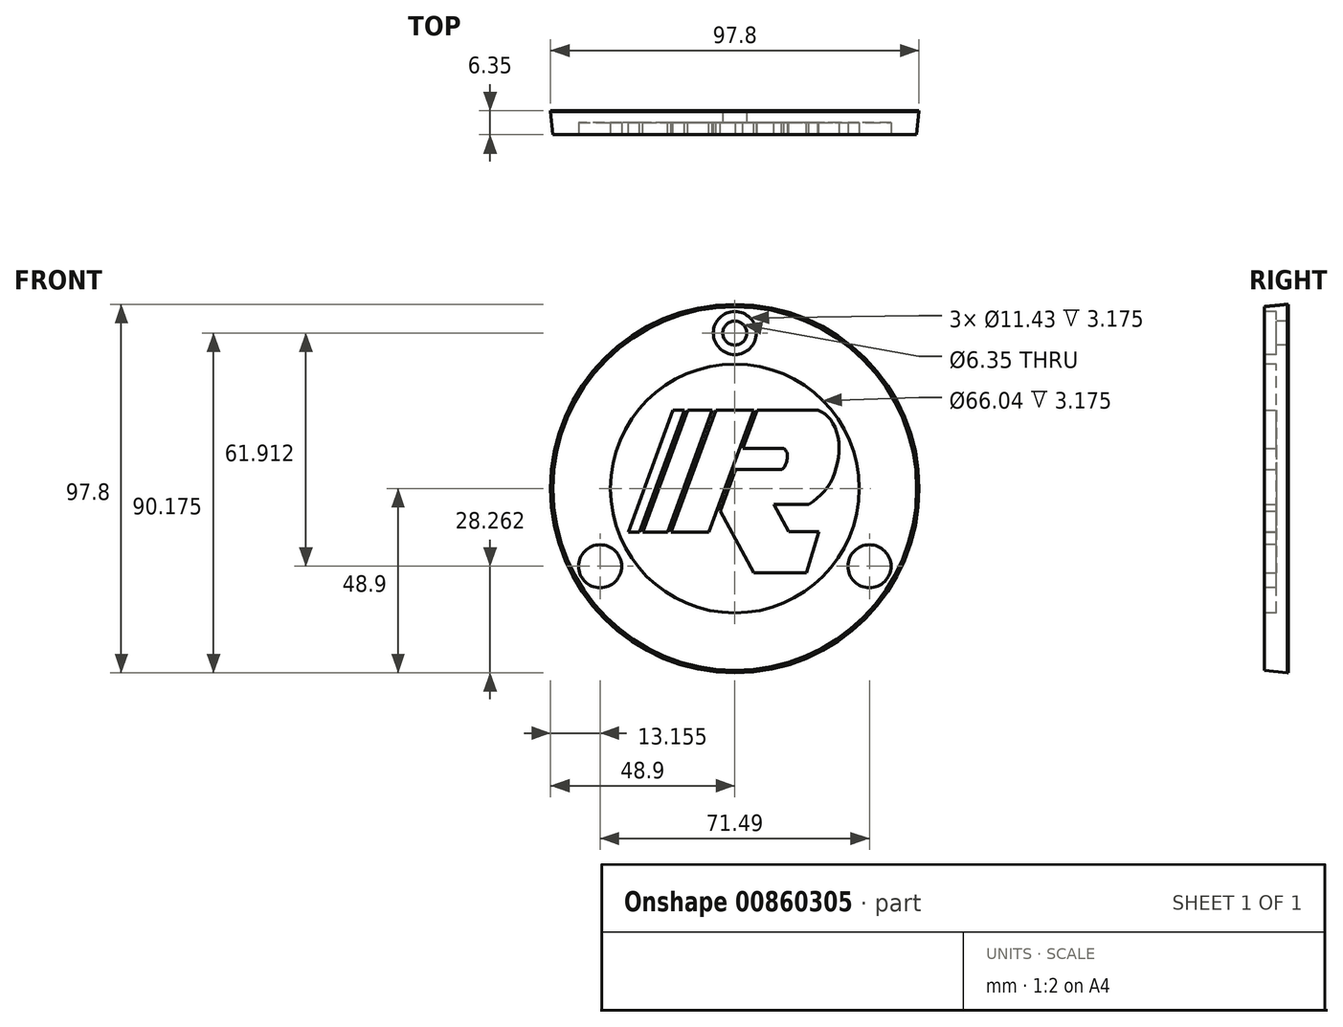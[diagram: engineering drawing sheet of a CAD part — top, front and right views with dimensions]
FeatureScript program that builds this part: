
annotation { "Feature Type Name" : "Feature", "Feature Type Description" : "" }
export const myFeature = defineFeature(function(context is Context, id is Id, definition is map)
    precondition{}
    {
        {
            var Q0;
            Q0=qCreatedBy(makeId("Front.planeOp"),FACE);
            var sketch = newSketch(context, id + "F0", { "sketchPlane" : qUnion([Q0])});
            skCircle(sketch, "E0", {"center": v(0, 0) * mm, "radius": 48.9 * mm});
            skSolve(sketch);
        }
        {
            var Q0;
            Q0 = qSketchRegion(id + "F0", true);
            extrude(context, id + "F1", {"entities" : qUnion([Q0]), "depth" : 6.35 * mm, "offsetDistance" : 25.4 * mm});
        }
        {
            var Q0;
            Q0=makeQuery(id+"F1.opExtrude","CAP_FACE",FACE,{"disambiguationData":[OSD([sQuery(id+"F0.wireOp",EDGE,"E0")])],"isStart":false});
            var sketch = newSketch(context, id + "F2", { "sketchPlane" : qUnion([Q0])});
            skCircle(sketch, "E1", {"center": v(0, 0) * mm, "radius": 33.02 * mm});
            skSolve(sketch);
        }
        {
            var Q0;
            Q0 = qSketchRegion(id + "F2", true);
            extrude(context, id + "F3", {"entities" : qUnion([Q0]), "operationType" : NewBodyOperationType.REMOVE, "oppositeDirection" : true, "depth" : 3.17 * mm, "offsetDistance" : 25.4 * mm});
        }
        {
            var Q0;
            Q0=makeQuery(id+"F1.opExtrude","CAP_FACE",FACE,{"disambiguationData":[OSD([sQuery(id+"F0.wireOp",EDGE,"E0")])],"isStart":false});
            var sketch = newSketch(context, id + "F4", { "sketchPlane" : qUnion([Q0])});
            skCircle(sketch, "E2", {"center": v(0, 41.28) * mm, "radius": 3.18 * mm});
            skPoint(sketch, "E3", {"position": v(0, 0) * mm});
            skSolve(sketch);
        }
        {
            var Q0;
            Q0 = qSketchRegion(id + "F4", true);
            extrude(context, id + "F5", {"entities" : qUnion([Q0]), "operationType" : NewBodyOperationType.REMOVE, "endBound" : BoundingType.THROUGH_ALL, "oppositeDirection" : true, "depth" : 25.4 * mm, "offsetDistance" : 25.4 * mm});
        }
        {
            var Q0;
            Q0=makeQuery(id+"F1.opExtrude","CAP_FACE",FACE,{"disambiguationData":[OSD([sQuery(id+"F0.wireOp",EDGE,"E0")])],"isStart":false});
            var sketch = newSketch(context, id + "F6", { "sketchPlane" : qUnion([Q0])});
            skCircle(sketch, "E4", {"center": v(0, 41.28) * mm, "radius": 5.72 * mm});
            skCircle(sketch, "E5", {"center": v(35.75, -20.64) * mm, "radius": 5.72 * mm});
            skCircle(sketch, "E6", {"center": v(-35.75, -20.64) * mm, "radius": 5.72 * mm});
            skSolve(sketch);
        }
        {
            var Q0;
            Q0 = qSketchRegion(id + "F6", true);
            extrude(context, id + "F7", {"entities" : qUnion([Q0]), "operationType" : NewBodyOperationType.REMOVE, "oppositeDirection" : true, "depth" : 3.17 * mm, "offsetDistance" : 25.4 * mm});
        }
        {
            var Q0;
            Q0=makeQuery(id+"F3.boolean.opBoolean","COPY",FACE,{"derivedFrom":makeQuery(id+"F3.opExtrude","CAP_FACE",FACE,{"disambiguationData":[OSD([sQuery(id+"F2.wireOp",EDGE,"E1")])],"isStart":false})});
            var sketch = newSketch(context, id + "F8", { "sketchPlane" : qUnion([Q0])});
            skLineSegment(sketch, "E7", {"start": v(-28.3, -11.58) * mm, "end": v(-16.4, 20.77) * mm});
            skLineSegment(sketch, "E8", {"start": v(-6.92, -11.58) * mm, "end": v(-16.9, -11.58) * mm});
            skLineSegment(sketch, "E9", {"start": v(-13.42, 20.77) * mm, "end": v(-25.32, -11.58) * mm});
            skLineSegment(sketch, "E10", {"start": v(-24.4, -11.58) * mm, "end": v(-12.5, 20.77) * mm});
            skLineSegment(sketch, "E11", {"start": v(-5.98, 20.77) * mm, "end": v(-17.89, -11.58) * mm});
            skLineSegment(sketch, "E12", {"start": v(-16.9, -11.58) * mm, "end": v(-5, 20.77) * mm});
            skLineSegment(sketch, "E13", {"start": v(4.98, 20.77) * mm, "end": v(-6.92, -11.58) * mm});
            skLineSegment(sketch, "E14", {"start": v(2.17, 10.67) * mm, "end": v(5.89, 20.77) * mm});
            skLineSegment(sketch, "E15", {"start": v(2.17, 10.67) * mm, "end": v(13, 10.67) * mm});
            skLineSegment(sketch, "E16", {"start": v(12.41, 5.01) * mm, "end": v(0.2, 5.01) * mm});
            skLineSegment(sketch, "E17", {"start": v(0.2, 5.01) * mm, "end": v(-3.84, -6) * mm});
            skLineSegment(sketch, "E18", {"start": v(-3.84, -6) * mm, "end": v(5.1, -22.4) * mm});
            skLineSegment(sketch, "E19", {"start": v(5.1, -22.4) * mm, "end": v(19.06, -22.4) * mm});
            skLineSegment(sketch, "E20", {"start": v(19.06, -22.4) * mm, "end": v(22.36, -11.5) * mm});
            skLineSegment(sketch, "E21", {"start": v(22.36, -11.5) * mm, "end": v(14.3, -11.5) * mm});
            skLineSegment(sketch, "E22", {"start": v(14.3, -11.5) * mm, "end": v(10.34, -4.23) * mm});
            skLineSegment(sketch, "E23", {"start": v(10.34, -4.23) * mm, "end": v(19.67, -4.23) * mm});
            skFitSpline(sketch, "E24", {"points": [v(22.06, 20.77) * mm, v(24.5, 19.29) * mm, v(26.33, 16.72) * mm, v(27.61, 12.4) * mm, v(27.37, 7.76) * mm, v(25.97, 2.76) * mm, v(23.22, -1.33) * mm, v(19.67, -4.23) * mm], "startDerivative": vector(22.06, -11.07) * mm, "endDerivative": vector(-24.89, -18.06) * mm});
            skLineSegment(sketch, "E25.trimOffspring", {"start": v(-13.42, 20.77) * mm, "end": v(-16.4, 20.77) * mm});
            skLineSegment(sketch, "E26.trimOffspring", {"start": v(-5.98, 20.77) * mm, "end": v(-12.5, 20.77) * mm});
            skLineSegment(sketch, "E27.trimOffspring", {"start": v(4.98, 20.77) * mm, "end": v(-5, 20.77) * mm});
            skLineSegment(sketch, "E28.trimOffspring", {"start": v(22.06, 20.77) * mm, "end": v(5.89, 20.77) * mm});
            skLineSegment(sketch, "E29.trimOffspring", {"start": v(-17.89, -11.58) * mm, "end": v(-24.4, -11.58) * mm});
            skLineSegment(sketch, "E30.trimOffspring", {"start": v(-25.32, -11.58) * mm, "end": v(-28.3, -11.58) * mm});
            skFitSpline(sketch, "E31", {"points": [v(13, 10.67) * mm, v(13.88, 9.37) * mm, v(13.83, 7.52) * mm, v(13, 5.57) * mm, v(12.41, 5.01) * mm], "startDerivative": vector(4.27, -4.82) * mm, "endDerivative": vector(-3.21, -2.36) * mm});
            skSolve(sketch);
        }
        {
            var Q0;
            Q0 = qSketchRegion(id + "F8", true);
            extrude(context, id + "F9", {"entities" : qUnion([Q0]), "operationType" : NewBodyOperationType.ADD, "depth" : 3.17 * mm, "offsetDistance" : 25.4 * mm});
        }
        {
            var Q0;
            Q0=qCreatedBy(makeId("Top.planeOp"),FACE);
            var sketch = newSketch(context, id + "F10", { "sketchPlane" : qUnion([Q0])});
            skLineSegment(sketch, "E32", {"start": v(48.91, 0) * mm, "end": v(48.28, -6.4) * mm});
            skLineSegment(sketch, "E33", {"start": v(48.28, -6.4) * mm, "end": v(48.91, -6.4) * mm});
            skLineSegment(sketch, "E34", {"start": v(48.91, -6.4) * mm, "end": v(48.91, 0) * mm});
            skLineSegment(sketch, "E35", {"start": v(0, 0) * mm, "end": v(0, -6.83) * mm});
            skSolve(sketch);
        }
        {
            var Q0;
            Q0 = qSketchRegion(id + "F10", true);
            var Q1;
            Q1=sQuery(id+"F10.wireOp",EDGE,"E35");
            revolve(context, id + "F11", {"operationType" : NewBodyOperationType.REMOVE, "surfaceOperationType" : NewSurfaceOperationType.NEW, "entities" : qUnion([Q0]), "axis" : qUnion([Q1]), "revolveType" : RevolveType.FULL});
        }
    });
